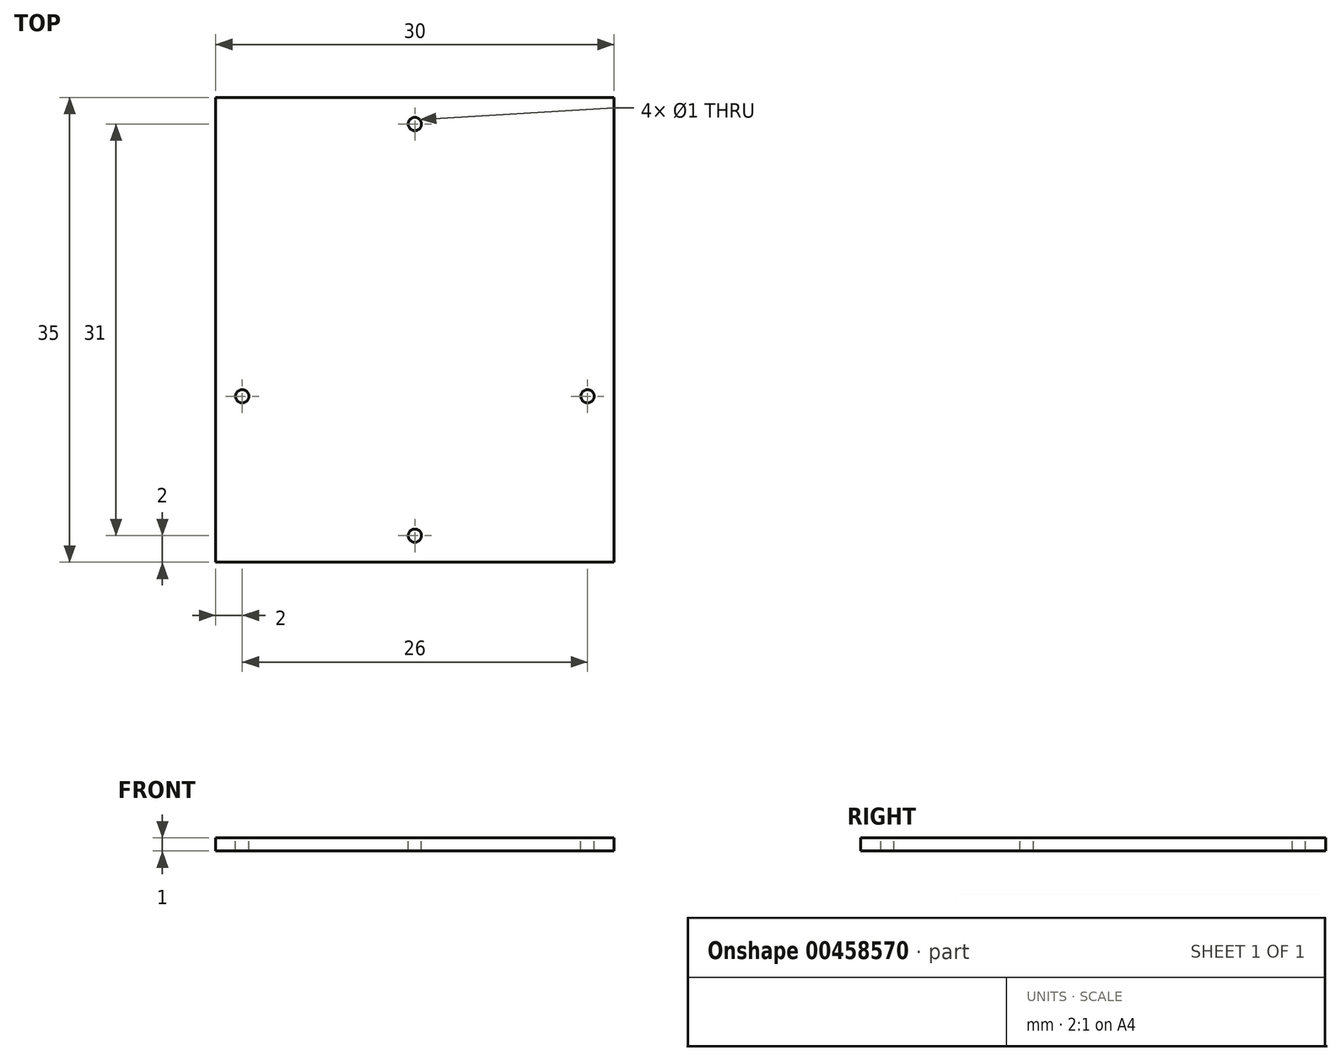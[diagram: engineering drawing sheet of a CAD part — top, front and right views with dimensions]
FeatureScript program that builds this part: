
annotation { "Feature Type Name" : "Feature", "Feature Type Description" : "" }
export const myFeature = defineFeature(function(context is Context, id is Id, definition is map)
    precondition{}
    {
        {
            var Q0;
            Q0=qCreatedBy(makeId("Top.planeOp"),FACE);
            var sketch = newSketch(context, id + "F0", { "sketchPlane" : qUnion([Q0])});
            skLineSegment(sketch, "E0.bottom", {"start": v(15, 17.5) * mm, "end": v(-15, 17.5) * mm});
            skLineSegment(sketch, "E0.top", {"start": v(15, -17.5) * mm, "end": v(-15, -17.5) * mm});
            skLineSegment(sketch, "E0.left", {"start": v(15, 17.5) * mm, "end": v(15, -17.5) * mm});
            skLineSegment(sketch, "E0.right", {"start": v(-15, 17.5) * mm, "end": v(-15, -17.5) * mm});
            skPoint(sketch, "E0.middle", {"position": v(0, 0) * mm});
            skSolve(sketch);
        }
        {
            var Q0;
            Q0=makeQuery(id+"F0.imprint","IMPRINT",FACE,{"disambiguationData":[TD([[makeQuery(id+"F0.imprint","IMPRINT",EDGE,{"derivedFrom":sQuery(id+"F0.wireOp",EDGE,"E0.bottom")}),1.0]])]});
            extrude(context, id + "F1", {"entities" : qUnion([Q0]), "depth" : 1 * mm, "offsetDistance" : 25 * mm});
        }
        {
            var Q0;
            Q0=makeQuery(id+"F1.opExtrude","CAP_FACE",FACE,{"disambiguationData":[OSD([sQuery(id+"F0.wireOp",EDGE,"E0.bottom"),sQuery(id+"F0.wireOp",EDGE,"E0.top"),sQuery(id+"F0.wireOp",EDGE,"E0.left"),sQuery(id+"F0.wireOp",EDGE,"E0.right")])],"isStart":false});
            var sketch = newSketch(context, id + "F2", { "sketchPlane" : qUnion([Q0])});
            skCircle(sketch, "E1", {"center": v(-13, -5) * mm, "radius": 0.5 * mm});
            skCircle(sketch, "E2", {"center": v(13, -5) * mm, "radius": 0.5 * mm});
            skCircle(sketch, "E3", {"center": v(0, 15.5) * mm, "radius": 0.5 * mm});
            skCircle(sketch, "E4", {"center": v(0, -15.5) * mm, "radius": 0.5 * mm});
            skSolve(sketch);
        }
        {
            var Q0;
            Q0 = qSketchRegion(id + "F2", true);
            extrude(context, id + "F3", {"entities" : qUnion([Q0]), "operationType" : NewBodyOperationType.REMOVE, "oppositeDirection" : true, "depth" : 1 * mm, "offsetDistance" : 25 * mm});
        }
    });
